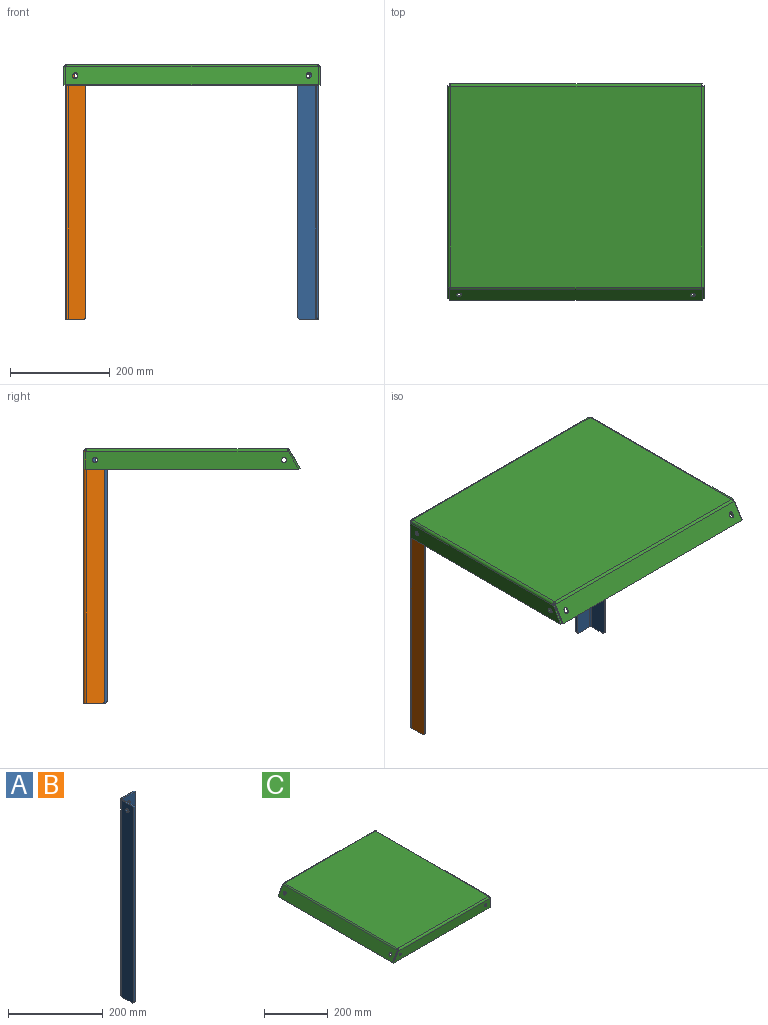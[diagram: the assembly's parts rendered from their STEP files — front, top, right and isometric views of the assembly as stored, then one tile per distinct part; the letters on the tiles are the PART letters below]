
ASSEMBLY  parts=3 mates=3
PART A: 18 faces, bbox 41.7x41.7x508 mm
  f0: plane 30.73x3.56mm, normal (0,0,-1), area 109.3mm2, adj f4,f5,f6,f14
  f1: plane 35.81x3.56mm, normal (0,0,1), area 127.4mm2, adj f3,f4,f5,f15
  f2: cylinder r=4.76mm len=9.53mm, axis (0,-1,0), area 106.4mm2, adj f4,f5
  f3: plane 502.92x3.56mm, normal (1,0,0), area 1788.4mm2, adj f1,f4,f5,f6
  f4: plane 508x35.81mm, normal (0,1,0), area 18116.7mm2, adj f0,f1,f2,f3,f6,f16
  f5: plane 508x35.81mm, normal (0,-1,0), area 18116.7mm2, adj f0,f1,f2,f3,f6,f17
  f6: cylinder r=5.08mm len=5.08mm, axis (0,-1,0), area 28.4mm2, adj f0,f3,f4,f5
  f7: plane 502.92x3.56mm, normal (0,-1,0), area 1788.4mm2, adj f8,f11,f12,f13
  f8: plane 35.81x3.56mm, normal (0,0,1), area 127.4mm2, adj f7,f11,f12,f15
  f9: cylinder r=4.76mm len=9.53mm, axis (1,0,0), area 106.4mm2, adj f11,f12
  f10: plane 30.73x3.56mm, normal (0,0,-1), area 109.3mm2, adj f11,f12,f13,f14
  f11: plane 508x35.81mm, normal (-1,0,0), area 18116.7mm2, adj f7,f8,f9,f10,f13,f16
  f12: plane 508x35.81mm, normal (1,0,0), area 18116.7mm2, adj f7,f8,f9,f10,f13,f17
  f13: cylinder r=5.08mm len=5.08mm, axis (-1,0,0), area 28.4mm2, adj f7,f10,f11,f12
  f14: plane 5.84x5.84mm, normal (0,0,-1), area 22.7mm2, adj f0,f10,f16,f17
  f15: plane 5.84x5.84mm, normal (0,0,1), area 22.7mm2, adj f1,f8,f16,f17
  f16: cylinder r=5.84mm len=508mm, axis (0,0,-1), area 4661.7mm2, adj f4,f11,f14,f15
  f17: cylinder r=2.29mm len=508mm, axis (0,0,-1), area 1824.1mm2, adj f5,f12,f14,f15
PART B: same geometry as A
PART C: 60 faces, bbox 435x515.1x41.7 mm
  f0: plane 503.43x402.79mm, normal (0,0,1), area 202777.9mm2, adj f13,f26,f39,f58
  f1: plane 503.43x402.79mm, normal (0,0,-1), area 202777.9mm2, adj f14,f27,f40,f59
  f2: plane 3.56x2.61mm, normal (0,0,1), area 9.3mm2, adj f3,f9,f10,f12
  f3: plane 35.81x20.68mm, normal (-0.87,0,0.5), area 147.1mm2, adj f2,f8,f9,f10
  f4: plane 3.56x2.26mm, normal (0,0,1), area 8mm2, adj f5,f9,f10,f11
  f5: plane 35.81x3.56mm, normal (1,0,0), area 127.4mm2, adj f4,f8,f9,f10
  f6: cylinder r=4.76mm len=9.53mm, axis (0,-1,0), area 106.4mm2, adj f9,f10
  f7: cylinder r=4.76mm len=9.53mm, axis (0,-1,0), area 106.4mm2, adj f9,f10
  f8: plane 428.34x3.56mm, normal (0,0,-1), area 1523.2mm2, adj f3,f5,f9,f10
  f9: plane 428.34x35.81mm, normal (0,1,0), area 14827.9mm2, adj f2,f3,f4,f5,f6,f7,f8,f13
  f10: plane 428.34x35.81mm, normal (0,-1,0), area 14827.9mm2, adj f2,f3,f4,f5,f6,f7,f8,f14
  f11: plane 5.84x5.84mm, normal (1,0,0), area 22.7mm2, adj f4,f13,f14,f37
  f12: plane 5.84x5.84mm, normal (-1,0,0), area 22.7mm2, adj f2,f13,f14,f56
  f13: cylinder r=5.84mm len=402.79mm, axis (1,0,0), area 3696.3mm2, adj f0,f9,f11,f12
  f14: cylinder r=2.29mm len=402.79mm, axis (1,0,0), area 1446.4mm2, adj f1,f10,f11,f12
  f15: plane 3.56x2.26mm, normal (0,0,1), area 8mm2, adj f18,f22,f23,f24
  f16: plane 35.81x20.68mm, normal (-0.87,0,0.5), area 147.1mm2, adj f17,f21,f22,f23
  f17: plane 428.34x3.56mm, normal (0,0,-1), area 1523.2mm2, adj f16,f18,f22,f23
  f18: plane 35.81x3.56mm, normal (1,0,0), area 127.4mm2, adj f15,f17,f22,f23
  f19: cylinder r=4.76mm len=9.53mm, axis (0,-1,0), area 106.4mm2, adj f22,f23
  f20: cylinder r=4.76mm len=9.53mm, axis (0,-1,0), area 106.4mm2, adj f22,f23
  f21: plane 3.56x2.61mm, normal (0,0,1), area 9.3mm2, adj f16,f22,f23,f25
  f22: plane 428.34x35.81mm, normal (0,-1,0), area 14827.9mm2, adj f15,f16,f17,f18,f19,f20,f21,f26
  f23: plane 428.34x35.81mm, normal (0,1,0), area 14827.9mm2, adj f15,f16,f17,f18,f19,f20,f21,f27
  f24: plane 5.84x5.84mm, normal (1,0,0), area 22.7mm2, adj f15,f26,f27,f38
  f25: plane 5.84x5.84mm, normal (-1,0,0), area 22.7mm2, adj f21,f26,f27,f57
  f26: cylinder r=5.84mm len=402.79mm, axis (1,0,0), area 3696.3mm2, adj f0,f22,f24,f25
  f27: cylinder r=2.29mm len=402.79mm, axis (1,0,0), area 1446.4mm2, adj f1,f23,f24,f25
  f28: plane 3.56x2.26mm, normal (0,0,1), area 8mm2, adj f31,f35,f36,f37
  f29: plane 35.81x3.56mm, normal (0,-1,0), area 127.4mm2, adj f30,f34,f35,f36
  f30: plane 507.95x3.56mm, normal (0,0,-1), area 1806.3mm2, adj f29,f31,f35,f36
  f31: plane 35.81x3.56mm, normal (0,1,0), area 127.4mm2, adj f28,f30,f35,f36
  f32: cylinder r=4.76mm len=9.53mm, axis (1,0,0), area 106.4mm2, adj f35,f36
  f33: cylinder r=4.76mm len=9.53mm, axis (1,0,0), area 106.4mm2, adj f35,f36
  f34: plane 3.56x2.26mm, normal (0,0,1), area 8mm2, adj f29,f35,f36,f38
  f35: plane 507.95x35.81mm, normal (1,0,0), area 18049.2mm2, adj f28,f29,f30,f31,f32,f33,f34,f39
  f36: plane 507.95x35.81mm, normal (-1,0,0), area 18049.2mm2, adj f28,f29,f30,f31,f32,f33,f34,f40
  f37: plane 5.84x5.84mm, normal (0,1,0), area 22.7mm2, adj f11,f28,f39,f40
  f38: plane 5.84x5.84mm, normal (0,-1,0), area 22.7mm2, adj f24,f34,f39,f40
  f39: cylinder r=5.84mm len=503.43mm, axis (0,1,0), area 4619.8mm2, adj f0,f35,f37,f38
  f40: cylinder r=2.29mm len=503.43mm, axis (0,1,0), area 1807.7mm2, adj f1,f36,f37,f38
  f41: plane 3.08x2.26mm, normal (0.5,0,0.87), area 8mm2, adj f42,f54,f55,f57
  f42: plane 38.74x24.42mm, normal (0,-1,0), area 151.7mm2, adj f41,f53,f54,f55
  f43: plane 3.08x2.26mm, normal (0.5,0,0.87), area 8mm2, adj f44,f54,f55,f56
  f44: plane 38.74x24.42mm, normal (0,1,0), area 151.7mm2, adj f43,f53,f54,f55
  f45: extruded ~9.52x6.54mm, area 56.7mm2, adj f46,f52,f54,f55
  f46: plane 4.11x3.66mm, normal (0,-1,0), area 7.5mm2, adj f45,f47,f54,f55
  f47: extruded ~9.52x6.65mm, area 57.8mm2, adj f46,f52,f54,f55
  f48: extruded ~9.52x6.54mm, area 56.7mm2, adj f49,f51,f54,f55
  f49: plane 4.11x3.66mm, normal (0,-1,0), area 7.5mm2, adj f48,f50,f54,f55
  f50: extruded ~9.52x6.65mm, area 57.8mm2, adj f49,f51,f54,f55
  f51: plane 4.05x3.66mm, normal (0,1,0), area 7.3mm2, adj f48,f50,f54,f55
  f52: plane 4.05x3.66mm, normal (0,1,0), area 7.3mm2, adj f45,f47,f54,f55
  f53: plane 507.95x3.08mm, normal (-0.5,0,-0.87), area 1806.3mm2, adj f42,f44,f54,f55
  f54: plane 507.95x36.96mm, normal (-0.87,0,0.5), area 21472.7mm2, adj f41,f42,f43,f44,f45,f46,f47,f48
  f55: plane 507.95x36.96mm, normal (0.87,0,-0.5), area 21472.8mm2, adj f41,f42,f43,f44,f45,f46,f47,f48
  f56: plane 5.06x4.7mm, normal (0,1,0), area 15.1mm2, adj f12,f43,f58,f59
  f57: plane 5.06x4.7mm, normal (0,-1,0), area 15.1mm2, adj f25,f41,f58,f59
  f58: cylinder r=5.84mm len=503.43mm, axis (0,1,0), area 3079.8mm2, adj f0,f54,f56,f57
  f59: cylinder r=2.29mm len=503.43mm, axis (0,1,0), area 1205.2mm2, adj f1,f55,f56,f57
PLACE A rot(axis=(0,0,-1),90deg) t=(-201.76,421.97,-307.91)mm
PLACE B rot(axis=(-0.51,0.7,0.5),0deg) t=(-561.97,568.69,-307.91)mm
PLACE C rot(axis=(0,0,1),90deg) t=(-706.2,267.02,-109.19)mm
MATE pin_slot A.f2 <-> C.f6  axis (1,0,0) through (-198.2,544.4,-86.78)mm
MATE pin_slot C.f1 <-> B.f15  axis (0,0,-1) through (-703.91,566.43,-67.73)mm
MATE slider B.f9 <-> C.f6  axis (1,0,0) through (-703.45,549.64,-86.78)mm
